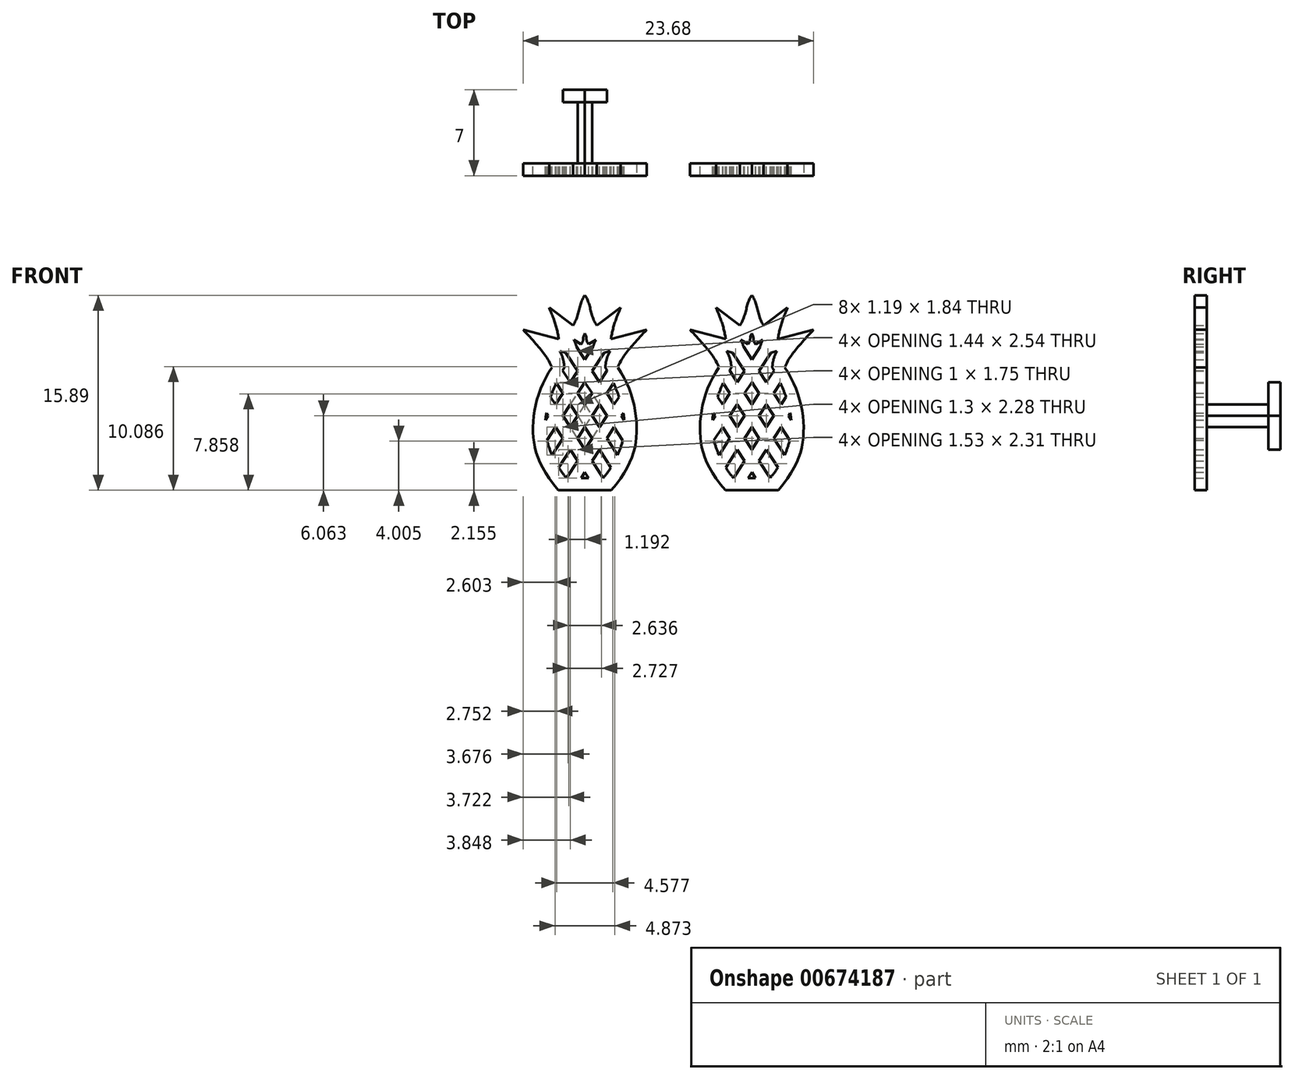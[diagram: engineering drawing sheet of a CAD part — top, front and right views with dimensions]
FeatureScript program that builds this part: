
annotation { "Feature Type Name" : "Feature", "Feature Type Description" : "" }
export const myFeature = defineFeature(function(context is Context, id is Id, definition is map)
    precondition{}
    {
        {
            var Q0;
            Q0=qCreatedBy(makeId("Front.planeOp"),FACE);
            var sketch = newSketch(context, id + "F0", { "sketchPlane" : qUnion([Q0])});
            skFitSpline(sketch, "E0", {"points": [v(-2.67, 5.04) * mm, v(-4.22, 0) * mm, v(-2.16, -4.96) * mm], "startDerivative": vector(-6.72, -9.41) * mm, "endDerivative": vector(9.65, -11.4) * mm});
            skLineSegment(sketch, "E1", {"start": v(-2.67, 5.04) * mm, "end": v(0, 5.04) * mm});
            skLineSegment(sketch, "E2", {"start": v(-2.16, -4.96) * mm, "end": v(0, -4.96) * mm});
            skPoint(sketch, "E3", {"position": v(-5.04, 8.14) * mm});
            skPoint(sketch, "E4", {"position": v(-2.91, 9.93) * mm});
            skLineSegment(sketch, "E5", {"start": v(-2.91, 9.93) * mm, "end": v(-0.98, 8.47) * mm});
            skLineSegment(sketch, "E6", {"start": v(-5.04, 8.14) * mm, "end": v(-2.13, 7.35) * mm});
            skFitSpline(sketch, "E7", {"points": [v(-2.67, 5.04) * mm, v(-5.04, 8.14) * mm], "startDerivative": vector(-1.28, 3.14) * mm, "endDerivative": vector(-3.24, 3.58) * mm});
            skFitSpline(sketch, "E8", {"points": [v(-2.13, 7.35) * mm, v(-2.91, 9.93) * mm], "startDerivative": vector(-0.34, 2.57) * mm, "endDerivative": vector(-1.34, 3.13) * mm});
            skFitSpline(sketch, "E9", {"points": [v(-0.98, 8.47) * mm, v(0, 10.93) * mm], "startDerivative": vector(1.68, 2.35) * mm, "endDerivative": vector(1.48, 1.9) * mm});
            skLineSegment(sketch, "E10", {"start": v(-1.5, -3.96) * mm, "end": v(0, -3.96) * mm});
            skPoint(sketch, "E11", {"position": v(-1.67, 5.04) * mm});
            skPoint(sketch, "E12", {"position": v(-2.04, 6.4) * mm});
            skPoint(sketch, "E13", {"position": v(-0.55, 6) * mm});
            skPoint(sketch, "E14", {"position": v(-0.9, 7.3) * mm});
            skFitSpline(sketch, "E15", {"points": [v(-1.67, 5.04) * mm, v(-2.04, 6.4) * mm], "startDerivative": vector(-0.03, 1.24) * mm, "endDerivative": vector(-0.77, 1.48) * mm});
            skFitSpline(sketch, "E16", {"points": [v(-0.55, 6) * mm, v(-0.9, 7.3) * mm], "startDerivative": vector(-0.06, 1.25) * mm, "endDerivative": vector(-0.7, 1.28) * mm});
            skLineSegment(sketch, "E17", {"start": v(-2.04, 6.4) * mm, "end": v(-0.55, 6) * mm});
            skPoint(sketch, "E18", {"position": v(-0.32, 6.95) * mm});
            skLineSegment(sketch, "E19", {"start": v(-0.32, 6.95) * mm, "end": v(-0.9, 7.3) * mm});
            skFitSpline(sketch, "E20", {"points": [v(-0.32, 6.95) * mm, v(0, 7.8) * mm], "startDerivative": vector(0.95, 0.85) * mm, "endDerivative": vector(0.73, 0.8) * mm});
            skFitSpline(sketch, "E21", {"points": [v(-1.5, -3.96) * mm, v(-3.22, 0) * mm, v(-1.67, 5.04) * mm], "startDerivative": vector(-3.78, 4.22) * mm, "endDerivative": vector(3.75, 6.6) * mm});
            skPoint(sketch, "E22", {"position": v(-0.3, -3.96) * mm});
            skFitSpline(sketch, "E23.MirrorCS", {"points": [v(0.98, 8.47) * mm, v(0, 10.93) * mm], "startDerivative": vector(-1.68, 2.35) * mm, "endDerivative": vector(-1.48, 1.9) * mm});
            skLineSegment(sketch, "E24.MirrorCS", {"start": v(2.91, 9.93) * mm, "end": v(0.98, 8.47) * mm});
            skFitSpline(sketch, "E25.MirrorCS", {"points": [v(2.13, 7.35) * mm, v(2.91, 9.93) * mm], "startDerivative": vector(0.34, 2.57) * mm, "endDerivative": vector(1.34, 3.13) * mm});
            skLineSegment(sketch, "E26.MirrorCS", {"start": v(5.04, 8.14) * mm, "end": v(2.13, 7.35) * mm});
            skFitSpline(sketch, "E27.MirrorCS", {"points": [v(2.67, 5.04) * mm, v(5.04, 8.14) * mm], "startDerivative": vector(1.28, 3.14) * mm, "endDerivative": vector(3.24, 3.58) * mm});
            skLineSegment(sketch, "E28.MirrorCS", {"start": v(2.67, 5.04) * mm, "end": v(0, 5.04) * mm});
            skFitSpline(sketch, "E29.MirrorCS", {"points": [v(1.5, -3.96) * mm, v(3.22, 0) * mm, v(1.67, 5.04) * mm], "startDerivative": vector(3.78, 4.22) * mm, "endDerivative": vector(-3.75, 6.6) * mm});
            skFitSpline(sketch, "E30.MirrorCS", {"points": [v(2.67, 5.04) * mm, v(4.22, 0) * mm, v(2.16, -4.96) * mm], "startDerivative": vector(6.72, -9.41) * mm, "endDerivative": vector(-9.65, -11.4) * mm});
            skLineSegment(sketch, "E31.MirrorCS", {"start": v(1.5, -3.96) * mm, "end": v(0, -3.96) * mm});
            skLineSegment(sketch, "E32.MirrorCS", {"start": v(2.16, -4.96) * mm, "end": v(0, -4.96) * mm});
            skFitSpline(sketch, "E33.MirrorCS", {"points": [v(0.32, 6.95) * mm, v(0, 7.8) * mm], "startDerivative": vector(-0.95, 0.85) * mm, "endDerivative": vector(-0.73, 0.8) * mm});
            skLineSegment(sketch, "E34.MirrorCS", {"start": v(0.32, 6.95) * mm, "end": v(0.9, 7.3) * mm});
            skFitSpline(sketch, "E35.MirrorCS", {"points": [v(0.55, 6) * mm, v(0.9, 7.3) * mm], "startDerivative": vector(0.06, 1.25) * mm, "endDerivative": vector(0.7, 1.28) * mm});
            skLineSegment(sketch, "E36.MirrorCS", {"start": v(2.04, 6.4) * mm, "end": v(0.55, 6) * mm});
            skFitSpline(sketch, "E37.MirrorCS", {"points": [v(1.67, 5.04) * mm, v(2.04, 6.4) * mm], "startDerivative": vector(0.03, 1.24) * mm, "endDerivative": vector(0.77, 1.48) * mm});
            skLineSegment(sketch, "E38", {"start": v(-1.5, -3.96) * mm, "end": v(2.79, 2.64) * mm});
            skLineSegment(sketch, "E39", {"start": v(-0.3, -3.96) * mm, "end": v(3.13, 1.34) * mm});
            skPoint(sketch, "E40", {"position": v(-2.13, -3.1) * mm});
            skPoint(sketch, "E41", {"position": v(-2.67, -2.1) * mm});
            skLineSegment(sketch, "E42", {"start": v(-2.13, -3.1) * mm, "end": v(2.33, 3.77) * mm});
            skLineSegment(sketch, "E43", {"start": v(-2.67, -2.1) * mm, "end": v(1.8, 4.8) * mm});
            skPoint(sketch, "E44", {"position": v(-3.08, -0.9) * mm});
            skPoint(sketch, "E45", {"position": v(-3.21, 0.75) * mm});
            skLineSegment(sketch, "E46", {"start": v(-3.08, -0.9) * mm, "end": v(1.56, 6.27) * mm});
            skLineSegment(sketch, "E47", {"start": v(-3.21, 0.75) * mm, "end": v(0.67, 6.73) * mm});
            skLineSegment(sketch, "E48", {"start": v(0.67, 6.73) * mm, "end": v(0.66, 6.61) * mm});
            skLineSegment(sketch, "E49.MirrorCS", {"start": v(0.3, -3.96) * mm, "end": v(-3.13, 1.34) * mm});
            skLineSegment(sketch, "E50.MirrorCS", {"start": v(1.5, -3.96) * mm, "end": v(-2.79, 2.64) * mm});
            skLineSegment(sketch, "E51.MirrorCS", {"start": v(2.13, -3.1) * mm, "end": v(-2.33, 3.77) * mm});
            skLineSegment(sketch, "E52.MirrorCS", {"start": v(2.67, -2.1) * mm, "end": v(-1.8, 4.8) * mm});
            skLineSegment(sketch, "E53.MirrorCS", {"start": v(3.08, -0.9) * mm, "end": v(-1.56, 6.27) * mm});
            skLineSegment(sketch, "E54.MirrorCS", {"start": v(3.21, 0.75) * mm, "end": v(-0.67, 6.73) * mm});
            skSolve(sketch);
        }
        {
            var Q0;
            Q0=makeQuery(id+"F0.imprint","IMPRINT",FACE,{"disambiguationData":[TD([[makeQuery(id+"F0.imprint","IMPRINT",EDGE,{"derivedFrom":sQuery(id+"F0.wireOp",EDGE,"E5")}),-1.0]])]});
            var Q1;
            {var subQ29=sQuery(id+"F0.wireOp",EDGE,"E0");Q1=makeQuery(id+"F0.imprint","IMPRINT",FACE,{"disambiguationData":[TD([[makeQuery(id+"F0.imprint","IMPRINT",EDGE,{"derivedFrom":subQ29}),1.0]])]});}
            var Q2;
            {var subQ1=sQuery(id+"F0.wireOp",EDGE,"E10");var subQ3=sQuery(id+"F0.wireOp",EDGE,"E39");var subQ4=makeQuery(id+"F0.imprint","INTERSECT",VERTEX,{"derivedFrom":[subQ1,subQ3]});Q2=makeQuery(id+"F0.imprint","IMPRINT",FACE,{"disambiguationData":[TD([[makeQuery(id+"F0.imprint","IMPRINT",EDGE,{"disambiguationData":[TD([[subQ4,-1.0]])],"derivedFrom":subQ3}),1.0]])]});}
            var Q3;
            {var subQ0=sQuery(id+"F0.wireOp",EDGE,"E49.MirrorCS");var subQ1=sQuery(id+"F0.wireOp",EDGE,"E38");var subQ2=makeQuery(id+"F0.imprint","INTERSECT",VERTEX,{"derivedFrom":[subQ1,subQ0]});Q3=makeQuery(id+"F0.imprint","IMPRINT",FACE,{"disambiguationData":[TD([[makeQuery(id+"F0.imprint","IMPRINT",EDGE,{"disambiguationData":[TD([[subQ2,-1.0]])],"derivedFrom":subQ1}),-1.0]])]});}
            var Q4;
            {var subQ0=sQuery(id+"F0.wireOp",EDGE,"E50.MirrorCS");var subQ1=sQuery(id+"F0.wireOp",EDGE,"E38");var subQ2=makeQuery(id+"F0.imprint","INTERSECT",VERTEX,{"derivedFrom":[subQ1,subQ0]});Q4=makeQuery(id+"F0.imprint","IMPRINT",FACE,{"disambiguationData":[TD([[makeQuery(id+"F0.imprint","IMPRINT",EDGE,{"disambiguationData":[TD([[subQ2,-1.0]])],"derivedFrom":subQ1}),-1.0]])]});}
            var Q5;
            {var subQ0=sQuery(id+"F0.wireOp",EDGE,"E51.MirrorCS");var subQ1=sQuery(id+"F0.wireOp",EDGE,"E38");var subQ2=makeQuery(id+"F0.imprint","INTERSECT",VERTEX,{"derivedFrom":[subQ1,subQ0]});Q5=makeQuery(id+"F0.imprint","IMPRINT",FACE,{"disambiguationData":[TD([[makeQuery(id+"F0.imprint","IMPRINT",EDGE,{"disambiguationData":[TD([[subQ2,-1.0]])],"derivedFrom":subQ1}),-1.0]])]});}
            var Q6;
            {var subQ0=sQuery(id+"F0.wireOp",EDGE,"E52.MirrorCS");var subQ1=sQuery(id+"F0.wireOp",EDGE,"E38");var subQ2=makeQuery(id+"F0.imprint","INTERSECT",VERTEX,{"derivedFrom":[subQ1,subQ0]});Q6=makeQuery(id+"F0.imprint","IMPRINT",FACE,{"disambiguationData":[TD([[makeQuery(id+"F0.imprint","IMPRINT",EDGE,{"disambiguationData":[TD([[subQ2,-1.0]])],"derivedFrom":subQ1}),-1.0]])]});}
            var Q7;
            {var subQ0=sQuery(id+"F0.wireOp",EDGE,"E53.MirrorCS");var subQ1=sQuery(id+"F0.wireOp",EDGE,"E38");var subQ2=makeQuery(id+"F0.imprint","INTERSECT",VERTEX,{"derivedFrom":[subQ1,subQ0]});Q7=makeQuery(id+"F0.imprint","IMPRINT",FACE,{"disambiguationData":[TD([[makeQuery(id+"F0.imprint","IMPRINT",EDGE,{"disambiguationData":[TD([[subQ2,-1.0]])],"derivedFrom":subQ1}),-1.0]])]});}
            var Q8;
            {var subQ0=sQuery(id+"F0.wireOp",EDGE,"E38");var subQ1=sQuery(id+"F0.wireOp",EDGE,"E29.MirrorCS");var subQ2=makeQuery(id+"F0.imprint","INTERSECT",VERTEX,{"derivedFrom":[subQ1,subQ0]});Q8=makeQuery(id+"F0.imprint","IMPRINT",FACE,{"disambiguationData":[TD([[makeQuery(id+"F0.imprint","IMPRINT",EDGE,{"disambiguationData":[TD([[subQ2,1.0]])],"derivedFrom":subQ1}),1.0]])]});}
            var Q9;
            {var subQ3=sQuery(id+"F0.wireOp",EDGE,"E49.MirrorCS");var subQ5=sQuery(id+"F0.wireOp",EDGE,"E39");var subQ6=makeQuery(id+"F0.imprint","INTERSECT",VERTEX,{"derivedFrom":[subQ5,subQ3]});Q9=makeQuery(id+"F0.imprint","IMPRINT",FACE,{"disambiguationData":[TD([[makeQuery(id+"F0.imprint","IMPRINT",EDGE,{"disambiguationData":[TD([[subQ6,-1.0]])],"derivedFrom":subQ5}),-1.0]])]});}
            var Q10;
            {var subQ0=sQuery(id+"F0.wireOp",EDGE,"E49.MirrorCS");var subQ1=sQuery(id+"F0.wireOp",EDGE,"E38");var subQ2=makeQuery(id+"F0.imprint","INTERSECT",VERTEX,{"derivedFrom":[subQ1,subQ0]});Q10=makeQuery(id+"F0.imprint","IMPRINT",FACE,{"disambiguationData":[TD([[makeQuery(id+"F0.imprint","IMPRINT",EDGE,{"disambiguationData":[TD([[subQ2,-1.0]])],"derivedFrom":subQ1}),1.0]])]});}
            var Q11;
            {var subQ0=sQuery(id+"F0.wireOp",EDGE,"E49.MirrorCS");var subQ1=sQuery(id+"F0.wireOp",EDGE,"E42");var subQ2=makeQuery(id+"F0.imprint","INTERSECT",VERTEX,{"derivedFrom":[subQ1,subQ0]});Q11=makeQuery(id+"F0.imprint","IMPRINT",FACE,{"disambiguationData":[TD([[makeQuery(id+"F0.imprint","IMPRINT",EDGE,{"disambiguationData":[TD([[subQ2,-1.0]])],"derivedFrom":subQ1}),1.0]])]});}
            var Q12;
            {var subQ0=sQuery(id+"F0.wireOp",EDGE,"E49.MirrorCS");var subQ1=sQuery(id+"F0.wireOp",EDGE,"E43");var subQ2=makeQuery(id+"F0.imprint","INTERSECT",VERTEX,{"derivedFrom":[subQ1,subQ0]});Q12=makeQuery(id+"F0.imprint","IMPRINT",FACE,{"disambiguationData":[TD([[makeQuery(id+"F0.imprint","IMPRINT",EDGE,{"disambiguationData":[TD([[subQ2,-1.0]])],"derivedFrom":subQ1}),1.0]])]});}
            var Q13;
            {var subQ0=sQuery(id+"F0.wireOp",EDGE,"E49.MirrorCS");var subQ1=sQuery(id+"F0.wireOp",EDGE,"E46");var subQ2=makeQuery(id+"F0.imprint","INTERSECT",VERTEX,{"derivedFrom":[subQ1,subQ0]});Q13=makeQuery(id+"F0.imprint","IMPRINT",FACE,{"disambiguationData":[TD([[makeQuery(id+"F0.imprint","IMPRINT",EDGE,{"disambiguationData":[TD([[subQ2,-1.0]])],"derivedFrom":subQ1}),1.0]])]});}
            var Q14;
            {var subQ0=sQuery(id+"F0.wireOp",EDGE,"E49.MirrorCS");var subQ1=sQuery(id+"F0.wireOp",EDGE,"E21");var subQ2=makeQuery(id+"F0.imprint","INTERSECT",VERTEX,{"derivedFrom":[subQ1,subQ0]});Q14=makeQuery(id+"F0.imprint","IMPRINT",FACE,{"disambiguationData":[TD([[makeQuery(id+"F0.imprint","IMPRINT",EDGE,{"disambiguationData":[TD([[subQ2,-1.0]])],"derivedFrom":subQ1}),-1.0]])]});}
            var Q15;
            {var subQ0=sQuery(id+"F0.wireOp",EDGE,"E42");var subQ1=sQuery(id+"F0.wireOp",EDGE,"E21");var subQ2=makeQuery(id+"F0.imprint","INTERSECT",VERTEX,{"derivedFrom":[subQ1,subQ0]});Q15=makeQuery(id+"F0.imprint","IMPRINT",FACE,{"disambiguationData":[TD([[makeQuery(id+"F0.imprint","IMPRINT",EDGE,{"disambiguationData":[TD([[subQ2,-1.0]])],"derivedFrom":subQ1}),-1.0]])]});}
            var Q16;
            {var subQ0=sQuery(id+"F0.wireOp",EDGE,"E50.MirrorCS");var subQ1=sQuery(id+"F0.wireOp",EDGE,"E42");var subQ2=makeQuery(id+"F0.imprint","INTERSECT",VERTEX,{"derivedFrom":[subQ1,subQ0]});Q16=makeQuery(id+"F0.imprint","IMPRINT",FACE,{"disambiguationData":[TD([[makeQuery(id+"F0.imprint","IMPRINT",EDGE,{"disambiguationData":[TD([[subQ2,-1.0]])],"derivedFrom":subQ1}),1.0]])]});}
            var Q17;
            {var subQ0=sQuery(id+"F0.wireOp",EDGE,"E51.MirrorCS");var subQ1=sQuery(id+"F0.wireOp",EDGE,"E42");var subQ2=makeQuery(id+"F0.imprint","INTERSECT",VERTEX,{"derivedFrom":[subQ1,subQ0]});Q17=makeQuery(id+"F0.imprint","IMPRINT",FACE,{"disambiguationData":[TD([[makeQuery(id+"F0.imprint","IMPRINT",EDGE,{"disambiguationData":[TD([[subQ2,-1.0]])],"derivedFrom":subQ1}),1.0]])]});}
            var Q18;
            {var subQ0=sQuery(id+"F0.wireOp",EDGE,"E52.MirrorCS");var subQ1=sQuery(id+"F0.wireOp",EDGE,"E42");var subQ2=makeQuery(id+"F0.imprint","INTERSECT",VERTEX,{"derivedFrom":[subQ1,subQ0]});Q18=makeQuery(id+"F0.imprint","IMPRINT",FACE,{"disambiguationData":[TD([[makeQuery(id+"F0.imprint","IMPRINT",EDGE,{"disambiguationData":[TD([[subQ2,-1.0]])],"derivedFrom":subQ1}),1.0]])]});}
            var Q19;
            {var subQ0=sQuery(id+"F0.wireOp",EDGE,"E53.MirrorCS");var subQ1=sQuery(id+"F0.wireOp",EDGE,"E42");var subQ2=makeQuery(id+"F0.imprint","INTERSECT",VERTEX,{"derivedFrom":[subQ1,subQ0]});Q19=makeQuery(id+"F0.imprint","IMPRINT",FACE,{"disambiguationData":[TD([[makeQuery(id+"F0.imprint","IMPRINT",EDGE,{"disambiguationData":[TD([[subQ2,-1.0]])],"derivedFrom":subQ1}),1.0]])]});}
            var Q20;
            {var subQ0=sQuery(id+"F0.wireOp",EDGE,"E42");var subQ1=sQuery(id+"F0.wireOp",EDGE,"E29.MirrorCS");var subQ2=makeQuery(id+"F0.imprint","INTERSECT",VERTEX,{"derivedFrom":[subQ1,subQ0]});Q20=makeQuery(id+"F0.imprint","IMPRINT",FACE,{"disambiguationData":[TD([[makeQuery(id+"F0.imprint","IMPRINT",EDGE,{"disambiguationData":[TD([[subQ2,-1.0]])],"derivedFrom":subQ1}),1.0]])]});}
            var Q21;
            {var subQ0=sQuery(id+"F0.wireOp",EDGE,"E46");var subQ1=sQuery(id+"F0.wireOp",EDGE,"E21");var subQ2=makeQuery(id+"F0.imprint","INTERSECT",VERTEX,{"derivedFrom":[subQ1,subQ0]});Q21=makeQuery(id+"F0.imprint","IMPRINT",FACE,{"disambiguationData":[TD([[makeQuery(id+"F0.imprint","IMPRINT",EDGE,{"disambiguationData":[TD([[subQ2,-1.0]])],"derivedFrom":subQ1}),-1.0]])]});}
            var Q22;
            {var subQ0=sQuery(id+"F0.wireOp",EDGE,"E50.MirrorCS");var subQ1=sQuery(id+"F0.wireOp",EDGE,"E46");var subQ2=makeQuery(id+"F0.imprint","INTERSECT",VERTEX,{"derivedFrom":[subQ1,subQ0]});Q22=makeQuery(id+"F0.imprint","IMPRINT",FACE,{"disambiguationData":[TD([[makeQuery(id+"F0.imprint","IMPRINT",EDGE,{"disambiguationData":[TD([[subQ2,-1.0]])],"derivedFrom":subQ1}),1.0]])]});}
            var Q23;
            {var subQ0=sQuery(id+"F0.wireOp",EDGE,"E51.MirrorCS");var subQ1=sQuery(id+"F0.wireOp",EDGE,"E46");var subQ2=makeQuery(id+"F0.imprint","INTERSECT",VERTEX,{"derivedFrom":[subQ1,subQ0]});Q23=makeQuery(id+"F0.imprint","IMPRINT",FACE,{"disambiguationData":[TD([[makeQuery(id+"F0.imprint","IMPRINT",EDGE,{"disambiguationData":[TD([[subQ2,-1.0]])],"derivedFrom":subQ1}),1.0]])]});}
            var Q24;
            {var subQ0=sQuery(id+"F0.wireOp",EDGE,"E52.MirrorCS");var subQ1=sQuery(id+"F0.wireOp",EDGE,"E46");var subQ2=makeQuery(id+"F0.imprint","INTERSECT",VERTEX,{"derivedFrom":[subQ1,subQ0]});Q24=makeQuery(id+"F0.imprint","IMPRINT",FACE,{"disambiguationData":[TD([[makeQuery(id+"F0.imprint","IMPRINT",EDGE,{"disambiguationData":[TD([[subQ2,-1.0]])],"derivedFrom":subQ1}),1.0]])]});}
            var Q25;
            {var subQ7=sQuery(id+"F0.wireOp",EDGE,"E28.MirrorCS");var subQ8=sQuery(id+"F0.wireOp",EDGE,"E1");var subQ9=makeQuery(id+"F0.imprint","INTERSECT",VERTEX,{"derivedFrom":[subQ8,subQ7]});Q25=makeQuery(id+"F0.imprint","IMPRINT",FACE,{"disambiguationData":[TD([[makeQuery(id+"F0.imprint","IMPRINT",EDGE,{"disambiguationData":[TD([[subQ9,1.0]])],"derivedFrom":subQ8}),-1.0]])]});}
            var Q26;
            {var subQ0=sQuery(id+"F0.wireOp",EDGE,"E46");var subQ3=sQuery(id+"F0.wireOp",EDGE,"E28.MirrorCS");var subQ4=makeQuery(id+"F0.imprint","INTERSECT",VERTEX,{"derivedFrom":[subQ3,subQ0]});Q26=makeQuery(id+"F0.imprint","IMPRINT",FACE,{"disambiguationData":[TD([[makeQuery(id+"F0.imprint","IMPRINT",EDGE,{"disambiguationData":[TD([[subQ4,-1.0]])],"derivedFrom":subQ3}),-1.0]])]});}
            var Q27;
            {var subQ1=sQuery(id+"F0.wireOp",EDGE,"E1");var subQ8=sQuery(id+"F0.wireOp",EDGE,"E53.MirrorCS");var subQ11=makeQuery(id+"F0.imprint","INTERSECT",VERTEX,{"derivedFrom":[subQ1,subQ8]});Q27=makeQuery(id+"F0.imprint","IMPRINT",FACE,{"disambiguationData":[TD([[makeQuery(id+"F0.imprint","IMPRINT",EDGE,{"disambiguationData":[TD([[subQ11,-1.0]])],"derivedFrom":subQ1}),1.0]])]});}
            var Q28;
            {var subQ0=sQuery(id+"F0.wireOp",EDGE,"E53.MirrorCS");var subQ1=sQuery(id+"F0.wireOp",EDGE,"E43");var subQ2=makeQuery(id+"F0.imprint","INTERSECT",VERTEX,{"derivedFrom":[subQ1,subQ0]});Q28=makeQuery(id+"F0.imprint","IMPRINT",FACE,{"disambiguationData":[TD([[makeQuery(id+"F0.imprint","IMPRINT",EDGE,{"disambiguationData":[TD([[subQ2,-1.0]])],"derivedFrom":subQ1}),1.0]])]});}
            var Q29;
            {var subQ0=sQuery(id+"F0.wireOp",EDGE,"E53.MirrorCS");var subQ1=sQuery(id+"F0.wireOp",EDGE,"E38");var subQ2=makeQuery(id+"F0.imprint","INTERSECT",VERTEX,{"derivedFrom":[subQ1,subQ0]});Q29=makeQuery(id+"F0.imprint","IMPRINT",FACE,{"disambiguationData":[TD([[makeQuery(id+"F0.imprint","IMPRINT",EDGE,{"disambiguationData":[TD([[subQ2,-1.0]])],"derivedFrom":subQ1}),1.0]])]});}
            var Q30;
            {var subQ0=sQuery(id+"F0.wireOp",EDGE,"E53.MirrorCS");var subQ1=sQuery(id+"F0.wireOp",EDGE,"E43");var subQ2=makeQuery(id+"F0.imprint","INTERSECT",VERTEX,{"derivedFrom":[subQ1,subQ0]});Q30=makeQuery(id+"F0.imprint","IMPRINT",FACE,{"disambiguationData":[TD([[makeQuery(id+"F0.imprint","IMPRINT",EDGE,{"disambiguationData":[TD([[subQ2,-1.0]])],"derivedFrom":subQ1}),1.0]])]});}
            var Q31;
            {var subQ0=sQuery(id+"F0.wireOp",EDGE,"E46");var subQ1=sQuery(id+"F0.wireOp",EDGE,"E28.MirrorCS");var subQ2=makeQuery(id+"F0.imprint","INTERSECT",VERTEX,{"derivedFrom":[subQ1,subQ0]});Q31=makeQuery(id+"F0.imprint","IMPRINT",FACE,{"disambiguationData":[TD([[makeQuery(id+"F0.imprint","IMPRINT",EDGE,{"disambiguationData":[TD([[subQ2,-1.0]])],"derivedFrom":subQ1}),1.0]])]});}
            var Q32;
            {var subQ0=sQuery(id+"F0.wireOp",EDGE,"E53.MirrorCS");var subQ1=sQuery(id+"F0.wireOp",EDGE,"E1");var subQ2=makeQuery(id+"F0.imprint","INTERSECT",VERTEX,{"derivedFrom":[subQ1,subQ0]});Q32=makeQuery(id+"F0.imprint","IMPRINT",FACE,{"disambiguationData":[TD([[makeQuery(id+"F0.imprint","IMPRINT",EDGE,{"disambiguationData":[TD([[subQ2,-1.0]])],"derivedFrom":subQ1}),-1.0]])]});}
            var Q33;
            {var subQ0=sQuery(id+"F0.wireOp",EDGE,"E28.MirrorCS");var subQ1=sQuery(id+"F0.wireOp",EDGE,"E1");var subQ2=makeQuery(id+"F0.imprint","INTERSECT",VERTEX,{"derivedFrom":[subQ1,subQ0]});Q33=makeQuery(id+"F0.imprint","IMPRINT",FACE,{"disambiguationData":[TD([[makeQuery(id+"F0.imprint","IMPRINT",EDGE,{"disambiguationData":[TD([[subQ2,1.0]])],"derivedFrom":subQ1}),1.0]])]});}
            var Q34;
            {var subQ0=sQuery(id+"F0.wireOp",EDGE,"E51.MirrorCS");var subQ1=sQuery(id+"F0.wireOp",EDGE,"E21");var subQ2=makeQuery(id+"F0.imprint","INTERSECT",VERTEX,{"derivedFrom":[subQ1,subQ0]});Q34=makeQuery(id+"F0.imprint","IMPRINT",FACE,{"disambiguationData":[TD([[makeQuery(id+"F0.imprint","IMPRINT",EDGE,{"disambiguationData":[TD([[subQ2,-1.0]])],"derivedFrom":subQ1}),-1.0]])]});}
            var Q35;
            {var subQ0=sQuery(id+"F0.wireOp",EDGE,"E51.MirrorCS");var subQ1=sQuery(id+"F0.wireOp",EDGE,"E43");var subQ2=makeQuery(id+"F0.imprint","INTERSECT",VERTEX,{"derivedFrom":[subQ1,subQ0]});Q35=makeQuery(id+"F0.imprint","IMPRINT",FACE,{"disambiguationData":[TD([[makeQuery(id+"F0.imprint","IMPRINT",EDGE,{"disambiguationData":[TD([[subQ2,-1.0]])],"derivedFrom":subQ1}),1.0]])]});}
            var Q36;
            {var subQ0=sQuery(id+"F0.wireOp",EDGE,"E51.MirrorCS");var subQ1=sQuery(id+"F0.wireOp",EDGE,"E38");var subQ2=makeQuery(id+"F0.imprint","INTERSECT",VERTEX,{"derivedFrom":[subQ1,subQ0]});Q36=makeQuery(id+"F0.imprint","IMPRINT",FACE,{"disambiguationData":[TD([[makeQuery(id+"F0.imprint","IMPRINT",EDGE,{"disambiguationData":[TD([[subQ2,-1.0]])],"derivedFrom":subQ1}),1.0]])]});}
            var Q37;
            {var subQ0=sQuery(id+"F0.wireOp",EDGE,"E51.MirrorCS");var subQ1=sQuery(id+"F0.wireOp",EDGE,"E29.MirrorCS");var subQ2=makeQuery(id+"F0.imprint","INTERSECT",VERTEX,{"derivedFrom":[subQ1,subQ0]});Q37=makeQuery(id+"F0.imprint","IMPRINT",FACE,{"disambiguationData":[TD([[makeQuery(id+"F0.imprint","IMPRINT",EDGE,{"disambiguationData":[TD([[subQ2,-1.0]])],"derivedFrom":subQ1}),1.0]])]});}
            var Q38;
            {var subQ0=sQuery(id+"F0.wireOp",EDGE,"E53.MirrorCS");var subQ1=sQuery(id+"F0.wireOp",EDGE,"E29.MirrorCS");var subQ2=makeQuery(id+"F0.imprint","INTERSECT",VERTEX,{"derivedFrom":[subQ1,subQ0]});Q38=makeQuery(id+"F0.imprint","IMPRINT",FACE,{"disambiguationData":[TD([[makeQuery(id+"F0.imprint","IMPRINT",EDGE,{"disambiguationData":[TD([[subQ2,-1.0]])],"derivedFrom":subQ1}),1.0]])]});}
            extrude(context, id + "F1", {"entities" : qUnion([Q0, Q1, Q2, Q3, Q4, Q5, Q6, Q7, Q8, Q9, Q10, Q11, Q12, Q13, Q14, Q15, Q16, Q17, Q18, Q19, Q20, Q21, Q22, Q23, Q24, Q25, Q26, Q27, Q28, Q29, Q30, Q31, Q32, Q33, Q34, Q35, Q36, Q37, Q38]), "depth" : 1 * mm, "offsetDistance" : 25 * mm});
        }
        {
            var Q0;
            Q0=makeQuery(id+"F1.opExtrude","CAP_FACE",FACE,{"disambiguationData":[OSD([sQuery(id+"F0.wireOp",EDGE,"E0"),sQuery(id+"F0.wireOp",EDGE,"E2"),sQuery(id+"F0.wireOp",EDGE,"E5"),sQuery(id+"F0.wireOp",EDGE,"E6"),sQuery(id+"F0.wireOp",EDGE,"E7"),sQuery(id+"F0.wireOp",EDGE,"E8"),sQuery(id+"F0.wireOp",EDGE,"E9"),sQuery(id+"F0.wireOp",EDGE,"E10"),sQuery(id+"F0.wireOp",EDGE,"E15"),sQuery(id+"F0.wireOp",EDGE,"E16"),sQuery(id+"F0.wireOp",EDGE,"E17"),sQuery(id+"F0.wireOp",EDGE,"E19"),sQuery(id+"F0.wireOp",EDGE,"E20"),sQuery(id+"F0.wireOp",EDGE,"E21"),sQuery(id+"F0.wireOp",EDGE,"E23.MirrorCS"),sQuery(id+"F0.wireOp",EDGE,"E24.MirrorCS"),sQuery(id+"F0.wireOp",EDGE,"E25.MirrorCS"),sQuery(id+"F0.wireOp",EDGE,"E26.MirrorCS"),sQuery(id+"F0.wireOp",EDGE,"E27.MirrorCS"),sQuery(id+"F0.wireOp",EDGE,"E29.MirrorCS"),sQuery(id+"F0.wireOp",EDGE,"E30.MirrorCS"),sQuery(id+"F0.wireOp",EDGE,"E31.MirrorCS"),sQuery(id+"F0.wireOp",EDGE,"E32.MirrorCS"),sQuery(id+"F0.wireOp",EDGE,"E33.MirrorCS"),sQuery(id+"F0.wireOp",EDGE,"E34.MirrorCS"),sQuery(id+"F0.wireOp",EDGE,"E35.MirrorCS"),sQuery(id+"F0.wireOp",EDGE,"E36.MirrorCS"),sQuery(id+"F0.wireOp",EDGE,"E37.MirrorCS"),sQuery(id+"F0.wireOp",EDGE,"E38"),sQuery(id+"F0.wireOp",EDGE,"E39"),sQuery(id+"F0.wireOp",EDGE,"E42"),sQuery(id+"F0.wireOp",EDGE,"E43"),sQuery(id+"F0.wireOp",EDGE,"E46"),sQuery(id+"F0.wireOp",EDGE,"E47"),sQuery(id+"F0.wireOp",EDGE,"E49.MirrorCS"),sQuery(id+"F0.wireOp",EDGE,"E50.MirrorCS"),sQuery(id+"F0.wireOp",EDGE,"E51.MirrorCS"),sQuery(id+"F0.wireOp",EDGE,"E52.MirrorCS"),sQuery(id+"F0.wireOp",EDGE,"E53.MirrorCS"),sQuery(id+"F0.wireOp",EDGE,"E54.MirrorCS")])],"isStart":true});
            var sketch = newSketch(context, id + "F2", { "sketchPlane" : qUnion([Q0])});
            skPoint(sketch, "E55", {"position": v(0, 0.18) * mm});
            skPoint(sketch, "E56", {"position": v(-0.6, 1.1) * mm});
            skPoint(sketch, "E57", {"position": v(0, 2.02) * mm});
            skPoint(sketch, "E58", {"position": v(0.6, 1.1) * mm});
            skLineSegment(sketch, "E59", {"start": v(0, 0.18) * mm, "end": v(-0.6, 1.1) * mm});
            skLineSegment(sketch, "E60", {"start": v(0, 2.02) * mm, "end": v(-0.6, 1.1) * mm});
            skLineSegment(sketch, "E61", {"start": v(0, 2.02) * mm, "end": v(0.6, 1.1) * mm});
            skLineSegment(sketch, "E62", {"start": v(0.6, 1.1) * mm, "end": v(0, 0.18) * mm});
            skLineSegment(sketch, "E63", {"start": v(-0.6, 2.94) * mm, "end": v(-1.2, 2.02) * mm});
            skLineSegment(sketch, "E64", {"start": v(-1.2, 2.02) * mm, "end": v(-1.79, 1.1) * mm});
            skLineSegment(sketch, "E65", {"start": v(-1.79, 1.1) * mm, "end": v(-1.2, 0.18) * mm});
            skLineSegment(sketch, "E66", {"start": v(-1.2, 0.18) * mm, "end": v(-0.6, -0.73) * mm});
            skLineSegment(sketch, "E67", {"start": v(-0.6, -0.73) * mm, "end": v(0, -1.65) * mm});
            skLineSegment(sketch, "E68", {"start": v(0, -1.65) * mm, "end": v(0.6, -0.73) * mm});
            skLineSegment(sketch, "E69", {"start": v(0.6, -0.73) * mm, "end": v(1.2, 0.18) * mm});
            skLineSegment(sketch, "E70", {"start": v(1.2, 0.18) * mm, "end": v(1.79, 1.1) * mm});
            skLineSegment(sketch, "E71", {"start": v(1.79, 1.1) * mm, "end": v(1.2, 2.02) * mm});
            skLineSegment(sketch, "E72", {"start": v(1.2, 2.02) * mm, "end": v(0.6, 2.94) * mm});
            skLineSegment(sketch, "E73", {"start": v(0.6, 2.94) * mm, "end": v(0, 3.86) * mm});
            skLineSegment(sketch, "E74", {"start": v(0, 3.86) * mm, "end": v(-0.6, 2.94) * mm});
            skSolve(sketch);
        }
        {
            var Q0;
            Q0=makeQuery(id+"F2.imprint","IMPRINT",FACE,{"disambiguationData":[TD([[makeQuery(id+"F2.imprint","IMPRINT",EDGE,{"derivedFrom":sQuery(id+"F2.wireOp",EDGE,"E59")}),-1.0]])]});
            extrude(context, id + "F3", {"entities" : qUnion([Q0]), "depth" : 5 * mm, "offsetDistance" : 25 * mm});
        }
        {
            var Q0;
            Q0 = qSketchRegion(id + "F2", true);
            var Q1;
            Q1=makeQuery(id+"F2.imprint","IMPRINT",FACE,{"disambiguationData":[TD([[makeQuery(id+"F2.imprint","IMPRINT",EDGE,{"derivedFrom":sQuery(id+"F2.wireOp",EDGE,"E59")}),-1.0]])]});
            extrude(context, id + "F4", {"entities" : qUnion([Q0, Q1]), "depth" : 1 * mm, "offsetDistance" : 25 * mm});
        }
        {
            var Q0;
            Q0=makeQuery(id+"F4.opExtrude","SWEPT_BODY",BODY,{"disambiguationData":[OSD([sQuery(id+"F2.wireOp",EDGE,"E63"),sQuery(id+"F2.wireOp",EDGE,"E64"),sQuery(id+"F2.wireOp",EDGE,"E65"),sQuery(id+"F2.wireOp",EDGE,"E66"),sQuery(id+"F2.wireOp",EDGE,"E67"),sQuery(id+"F2.wireOp",EDGE,"E68"),sQuery(id+"F2.wireOp",EDGE,"E69"),sQuery(id+"F2.wireOp",EDGE,"E70"),sQuery(id+"F2.wireOp",EDGE,"E71"),sQuery(id+"F2.wireOp",EDGE,"E72"),sQuery(id+"F2.wireOp",EDGE,"E73"),sQuery(id+"F2.wireOp",EDGE,"E74")])]});
            transform(context, id + "F5", {"entities" : qUnion([Q0]), "transformType" : TransformType.TRANSLATION_3D, "dx" : 0 * mm, "dy" : 5 * mm, "dz" : 0 * mm, "makeCopy" : false});
        }
        {
            var Q0;
            Q0=makeQuery(id+"F1.opExtrude","SWEPT_BODY",BODY,{"disambiguationData":[OSD([sQuery(id+"F0.wireOp",EDGE,"E0"),sQuery(id+"F0.wireOp",EDGE,"E2"),sQuery(id+"F0.wireOp",EDGE,"E5"),sQuery(id+"F0.wireOp",EDGE,"E6"),sQuery(id+"F0.wireOp",EDGE,"E7"),sQuery(id+"F0.wireOp",EDGE,"E8"),sQuery(id+"F0.wireOp",EDGE,"E9"),sQuery(id+"F0.wireOp",EDGE,"E10"),sQuery(id+"F0.wireOp",EDGE,"E15"),sQuery(id+"F0.wireOp",EDGE,"E16"),sQuery(id+"F0.wireOp",EDGE,"E17"),sQuery(id+"F0.wireOp",EDGE,"E19"),sQuery(id+"F0.wireOp",EDGE,"E20"),sQuery(id+"F0.wireOp",EDGE,"E21"),sQuery(id+"F0.wireOp",EDGE,"E23.MirrorCS"),sQuery(id+"F0.wireOp",EDGE,"E24.MirrorCS"),sQuery(id+"F0.wireOp",EDGE,"E25.MirrorCS"),sQuery(id+"F0.wireOp",EDGE,"E26.MirrorCS"),sQuery(id+"F0.wireOp",EDGE,"E27.MirrorCS"),sQuery(id+"F0.wireOp",EDGE,"E29.MirrorCS"),sQuery(id+"F0.wireOp",EDGE,"E30.MirrorCS"),sQuery(id+"F0.wireOp",EDGE,"E31.MirrorCS"),sQuery(id+"F0.wireOp",EDGE,"E32.MirrorCS"),sQuery(id+"F0.wireOp",EDGE,"E33.MirrorCS"),sQuery(id+"F0.wireOp",EDGE,"E34.MirrorCS"),sQuery(id+"F0.wireOp",EDGE,"E35.MirrorCS"),sQuery(id+"F0.wireOp",EDGE,"E36.MirrorCS"),sQuery(id+"F0.wireOp",EDGE,"E37.MirrorCS"),sQuery(id+"F0.wireOp",EDGE,"E38"),sQuery(id+"F0.wireOp",EDGE,"E39"),sQuery(id+"F0.wireOp",EDGE,"E42"),sQuery(id+"F0.wireOp",EDGE,"E43"),sQuery(id+"F0.wireOp",EDGE,"E46"),sQuery(id+"F0.wireOp",EDGE,"E47"),sQuery(id+"F0.wireOp",EDGE,"E49.MirrorCS"),sQuery(id+"F0.wireOp",EDGE,"E50.MirrorCS"),sQuery(id+"F0.wireOp",EDGE,"E51.MirrorCS"),sQuery(id+"F0.wireOp",EDGE,"E52.MirrorCS"),sQuery(id+"F0.wireOp",EDGE,"E53.MirrorCS"),sQuery(id+"F0.wireOp",EDGE,"E54.MirrorCS")])]});
            transform(context, id + "F6", {"entities" : qUnion([Q0]), "transformType" : TransformType.TRANSLATION_3D, "dx" : 13.6 * mm, "dy" : 0 * mm, "dz" : 0 * mm, "makeCopy" : true});
        }
    });
